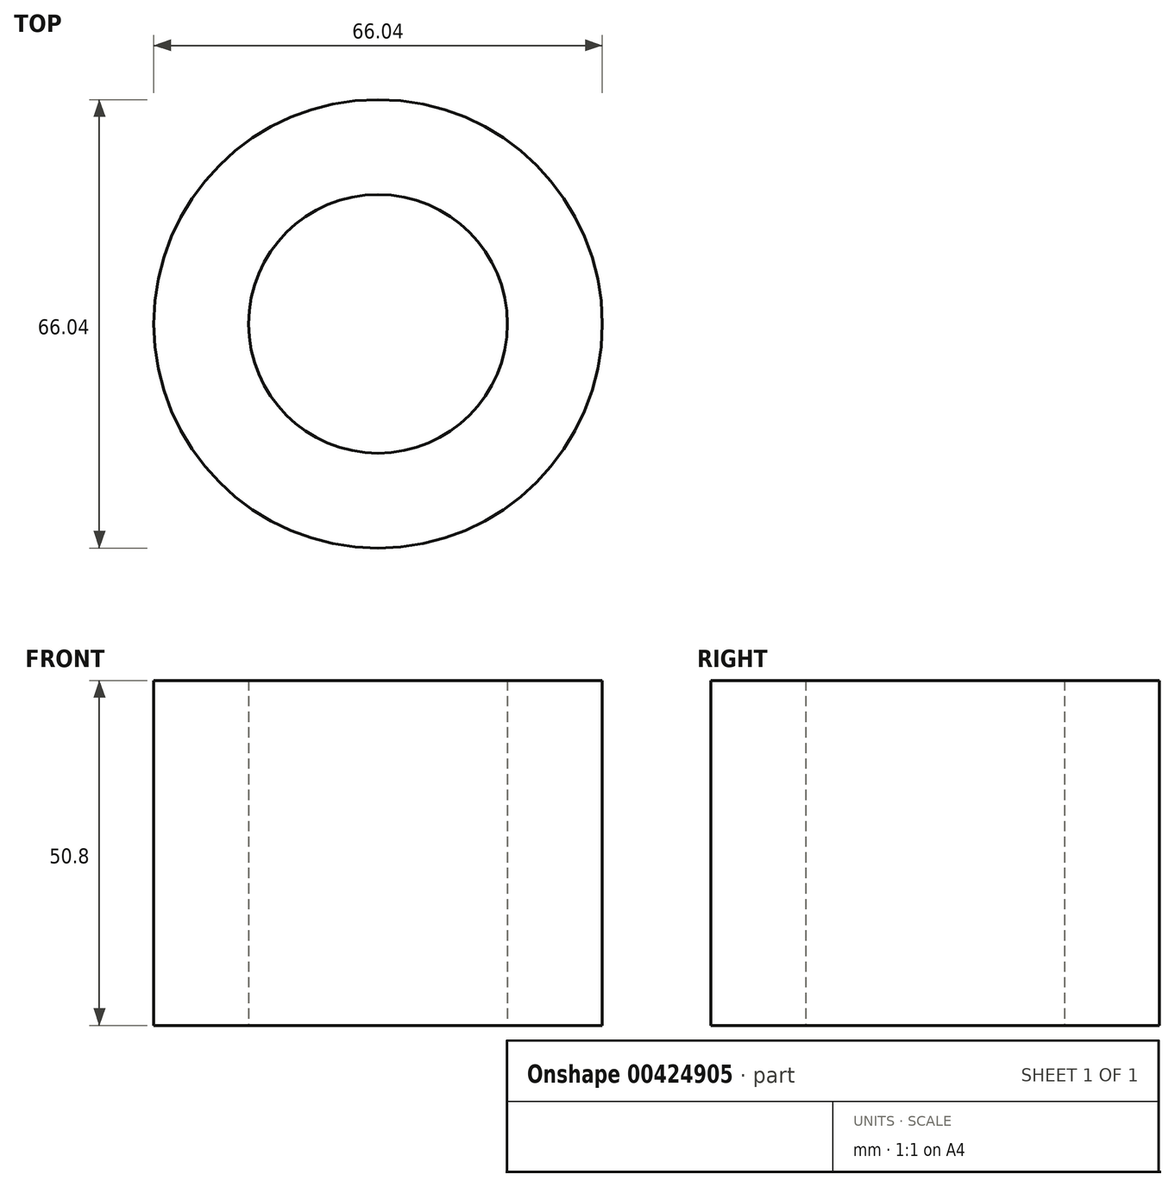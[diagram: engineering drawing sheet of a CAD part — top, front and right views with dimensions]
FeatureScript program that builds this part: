
annotation { "Feature Type Name" : "Feature", "Feature Type Description" : "" }
export const myFeature = defineFeature(function(context is Context, id is Id, definition is map)
    precondition{}
    {
        {
            var Q0;
            Q0=qCreatedBy(makeId("Top.planeOp"),FACE);
            var sketch = newSketch(context, id + "F0", { "sketchPlane" : qUnion([Q0])});
            skCircle(sketch, "E0", {"center": v(0, 0) * mm, "radius": 33.02 * mm});
            skCircle(sketch, "E1", {"center": v(0, 0) * mm, "radius": 19.05 * mm});
            skSolve(sketch);
        }
        {
            var Q0;
            Q0 = qSketchRegion(id + "F0", true);
            extrude(context, id + "F1", {"entities" : qUnion([Q0]), "depth" : 50.8 * mm});
        }
    });
